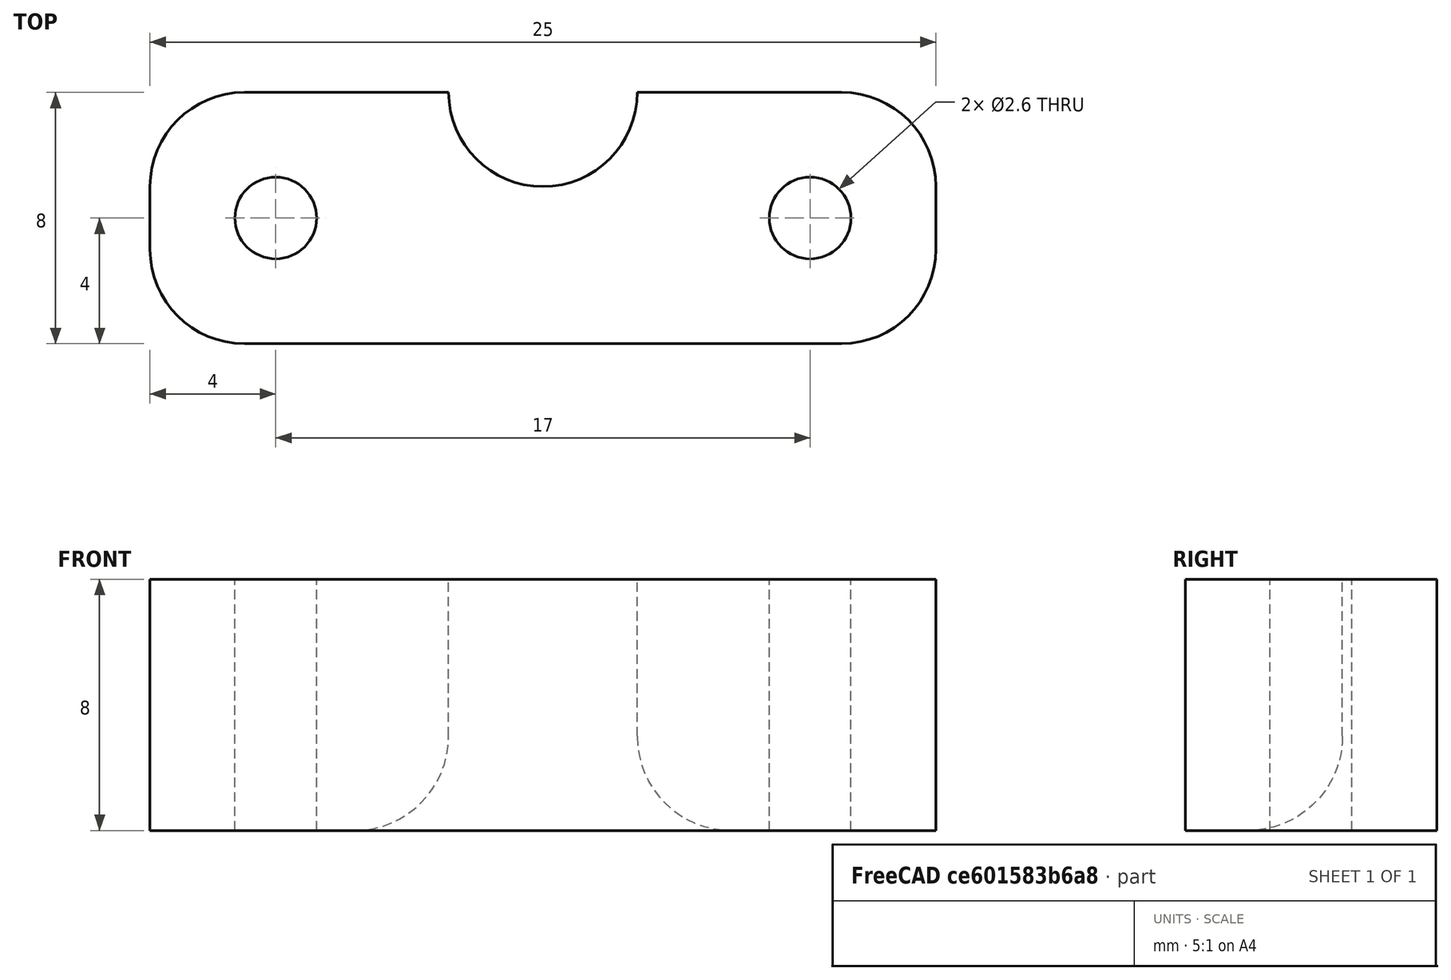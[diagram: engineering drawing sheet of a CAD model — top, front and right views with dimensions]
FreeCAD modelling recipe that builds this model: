
FCSTD DOCUMENT  (FreeCAD 0.18.3R)
Label: cablegrip
License: All rights reserved
LicenseURL: http://en.wikipedia.org/wiki/All_rights_reserved
objects: Part::Cylinder×3, Part::Cut×2, Part::Fillet×2, Part::Box×1, Part::MultiFuse×1
note: 9 computed .brp shape members not serialized (recipe doc carries the construction recipe); baked Part::Feature solids carry a one-line shape summary decoded from their .brp

FEATURE [Part::Box] Box  label="Cube"
  AttacherType = Attacher::AttachEngine3D
  Height = 8
  Length = 25
  Width = 8
FEATURE [Part::Cylinder] Cylinder
  Angle = 360
  AttacherType = Attacher::AttachEngine3D
  Height = 10
  Placement = pos=(4,4,-1) rot=(0,0,1;0rad)
  Radius = 1.3
FEATURE [Part::Cylinder] Cylinder001
  Angle = 360
  AttacherType = Attacher::AttachEngine3D
  Height = 10
  Placement = pos=(21,4,-1) rot=(0,0,1;0rad)
  Radius = 1.3
FEATURE [Part::MultiFuse] Fusion
  Shapes = -> [Cylinder,Cylinder001]
FEATURE [Part::Cut] Cut
  Base = -> Box
  Tool = -> Fusion
FEATURE [Part::Fillet] Fillet
  Base = -> Cut
  Edges = 4 edges r=3: [Edge1,Edge3,Edge6,Edge13]
FEATURE [Part::Cylinder] Cylinder002
  Angle = 360
  AttacherType = Attacher::AttachEngine3D
  Height = 10
  Placement = pos=(12.5,8,-1) rot=(0,0,1;0rad)
  Radius = 3
FEATURE [Part::Cut] Cut001
  Base = -> Fillet
  Tool = -> Cylinder002
FEATURE [Part::Fillet] Fillet001
  Base = -> Cut001
  Edges = 1 edges r=3: [Edge21]
